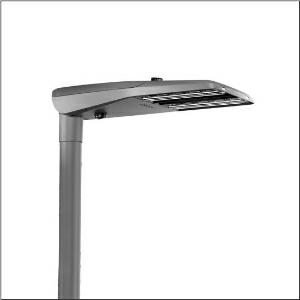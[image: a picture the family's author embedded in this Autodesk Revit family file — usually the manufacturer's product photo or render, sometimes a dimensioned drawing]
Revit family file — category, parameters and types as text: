
# Revit family: streetlight_sl_11_iq_midi___st1_2a_5xc3a41y08me_bddd
name_source: partatom
category: Lighting Fixtures
units: mm (PartAtom-declared; Revit-internal decimal feet)

## family parameters
Cut with Voids When Loaded = No
Host = Face
Light Source = No
Part Type = Normal
Room Calculation Point = No
Round Connector Dimension = Use Diameter
Shared = No

## types (1)
- --- (1 x LED, 18900 lm, 122.6 W, 4000K)
    Apparent Load = 123 VA
    CIE Flux Codes = 32 70 96 100 100
    Color Rendering = 70
    Color Temperature = 4000K
    Default Elevation = 1800 mm
    Description = Streetlight SL 11 iQ midi, mast luminaire, primary light control with 3 zone facetted reflector, of plastic, silver coated, highly specular, primary optical cover: cover, of PMMA, transparent, light distribution: ST1.2a, light emission: direct distribution, primary light characteristic: asymmetric, installation type: post-top, side-entry, LED, High Power LED, rated luminous flux: 18.900lm, luminous efficacy: 154lm/W, light colour: 740, colour temperature: 4000K, control: presetting dimming logarithmic, Street-Remote, Auto-Match, Temp-Guard, Lumen-Switch, Night-Set, Smart-Wire, Light-Fading, Desk-Remote (wireless, voltage-free reading and setting of iQ features in the workshop via application-optimized NFC function/RFID function), optimised constant luminous flux control (CLO 2.0), with cable H07RN-F 5x 1.5mm², mains connection: 220..240V, AC, 50/60Hz, connection cable pre-assembled, cable length: 12,5m, start of lifetime: 123W, end of service life: 130W, reduction: 56W, luminaire housing, of diecast aluminium, powder-coated, Siteco® metallic grey (DB 702S), please order mast flange separately, inclination adjustable without tools: 0°, 5°, 10°, 15° (post-top) | 0°, -5°, -10°, -15° (side-entry), sealing non-destructively replaceable, multi-level sealing system, length: 780mm, width: 376mm, height: 118mm, spigot size: 60/76mm (post-top) and 42/60/76mm (side-entry), mast flange for spigot size: 42mm: 5XC10008XM4, 60mm: 5XC10008XM2, 76/60mm: 5XC10108XM1, equipment: Power, Smart Interface below and above, protection rating (complete): IP66, insulation class (complete): insulation class II (safety insulation), certification: CE, ENEC in preparation, impact resistance: IK09, permissible operating ambient temperature for outdoor applications: -25..+50°C, standard-compliant lighting for roads and squares, packaging unit: 1 piece

Light Distribution: ST1.2a
    Height = 118 mm
    Lamp = 1 x LED
    Lamp Light Flux = 18900 lm
    Lamp Power = 122.6 W
    Lamp count = 1
    Length = 780 mm
    Luminous efficacy = 154 lm/W
    Manufacturer = Siteco
    ModVariant = No
    Model = 5XC3A41Y08ME
    Number of Poles = 1
    OnlyDefault = Yes
    Power Factor = 1
    Product Name = Streetlight SL 11 iQ midi | ST1.2a
    Product group = mast luminaire | pylon top
    ProductGroupID = 6100
    Protection Class = Protection class II
    Protection Degree = IP 66
    RLX_Detail_Level = 1
    RlxData = <blob elided: 69565 chars, md5=5b9935f7>
    Socket = socket
    Standby Power = 0 W
    System Light Flux = 18900 lm
    System Power = 123 W
    Type Comments = factory setting: luminous flux: 100 % | dim-lin: 254 | 552 mA
    Type Image = l_1004429.jpg
    URL = http://relux.com
    VarID = @adj_043581
    Voltage = 0 V
    Weight = 0.00 kg
    Width = 376 mm

## geometry (parser evidence)
native form markers: Blend x4, Sweep x10
no freeform markers — native parametric forms only
